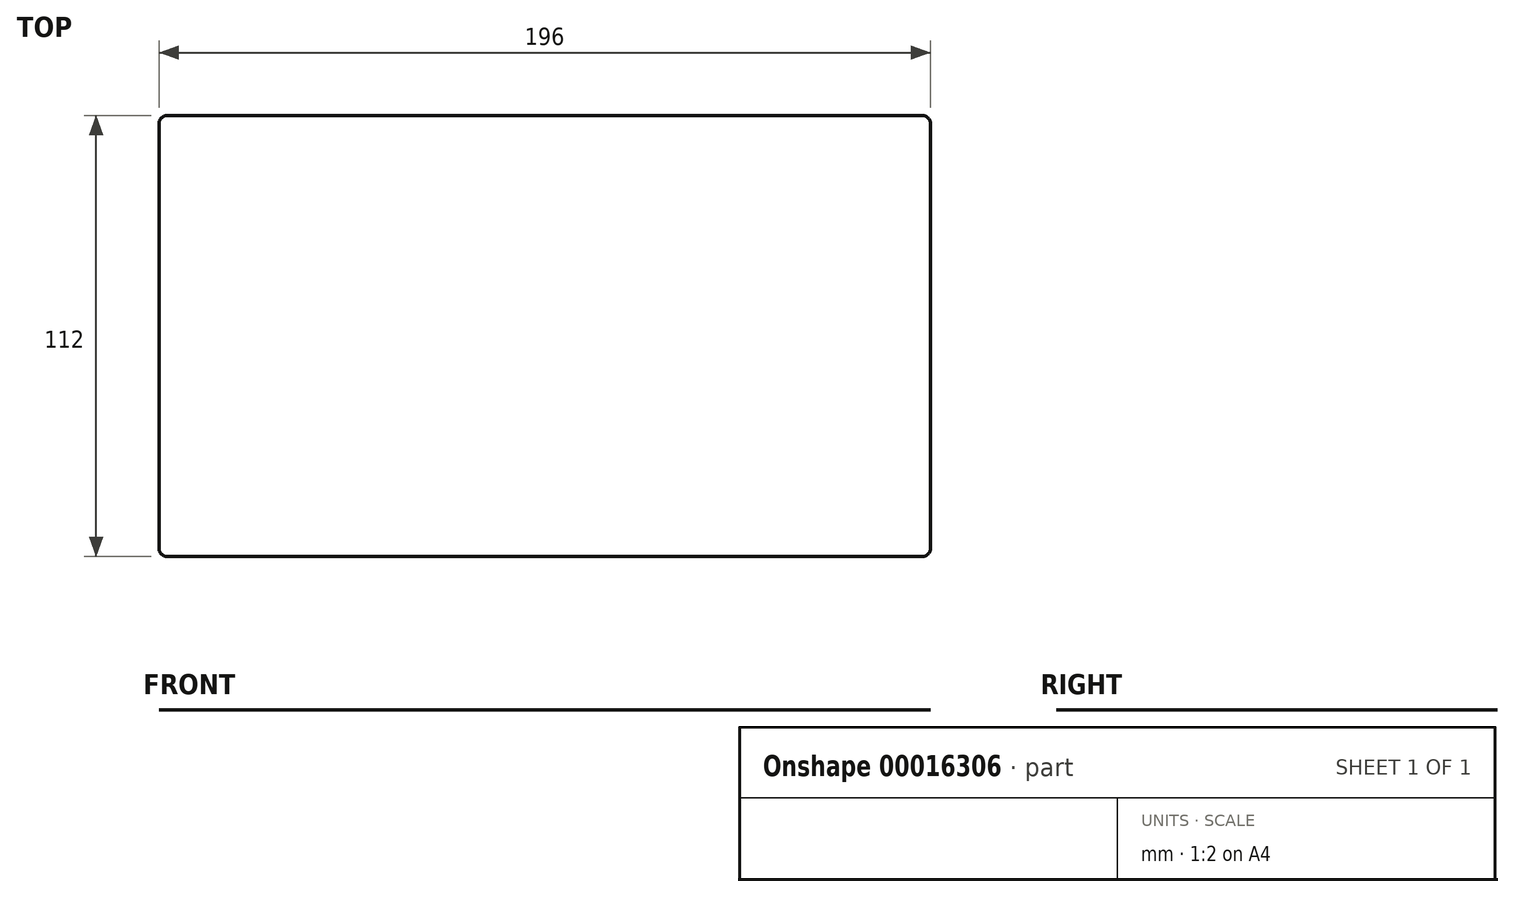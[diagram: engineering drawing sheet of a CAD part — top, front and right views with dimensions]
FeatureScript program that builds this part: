
annotation { "Feature Type Name" : "Feature", "Feature Type Description" : "" }
export const myFeature = defineFeature(function(context is Context, id is Id, definition is map)
    precondition{}
    {
        {
            var Q0;
            Q0=qCreatedBy(makeId("Top.planeOp"),FACE);
            var sketch = newSketch(context, id + "F0", { "sketchPlane" : qUnion([Q0])});
            skLineSegment(sketch, "E0.bottom", {"start": v(96, 54) * mm, "end": v(-96, 54) * mm, "construction": true});
            skLineSegment(sketch, "E0.top", {"start": v(96, -54) * mm, "end": v(-96, -54) * mm, "construction": true});
            skLineSegment(sketch, "E0.left", {"start": v(96, 54) * mm, "end": v(96, -54) * mm, "construction": true});
            skLineSegment(sketch, "E0.right", {"start": v(-96, 54) * mm, "end": v(-96, -54) * mm, "construction": true});
            skPoint(sketch, "E0.middle", {"position": v(0, 0) * mm});
            skLineSegment(sketch, "E1.0", {"start": v(96, 56) * mm, "end": v(-96, 56) * mm});
            skLineSegment(sketch, "E1.1", {"start": v(98, 54) * mm, "end": v(98, -54) * mm});
            skLineSegment(sketch, "E1.2", {"start": v(96, -56) * mm, "end": v(-96, -56) * mm});
            skLineSegment(sketch, "E1.3", {"start": v(-98, 54) * mm, "end": v(-98, -54) * mm});
            skPoint(sketch, "E2.visualSharp", {"position": v(-98, 56) * mm});
            skArc(sketch, "E2.filletArc", {"start": v(-96, 56) * mm, "mid": v(-97.41, 55.41) * mm, "end": v(-98, 54) * mm});
            skPoint(sketch, "E3.visualSharp", {"position": v(-98, -56) * mm});
            skArc(sketch, "E3.filletArc", {"start": v(-98, -54) * mm, "mid": v(-97.41, -55.41) * mm, "end": v(-96, -56) * mm});
            skPoint(sketch, "E4.visualSharp", {"position": v(98, -56) * mm});
            skArc(sketch, "E4.filletArc", {"start": v(96, -56) * mm, "mid": v(97.41, -55.41) * mm, "end": v(98, -54) * mm});
            skPoint(sketch, "E5.visualSharp", {"position": v(98, 56) * mm});
            skArc(sketch, "E5.filletArc", {"start": v(98, 54) * mm, "mid": v(97.41, 55.41) * mm, "end": v(96, 56) * mm});
            skSolve(sketch);
        }
        {
            var Q0;
            Q0=makeQuery(id+"F0.imprint","IMPRINT",FACE,{"disambiguationData":[TD([[makeQuery(id+"F0.imprint","IMPRINT",EDGE,{"derivedFrom":sQuery(id+"F0.wireOp",EDGE,"E1.0")}),1.0]])]});
            extrude(context, id + "F1", {"entities" : qUnion([Q0]), "depth" : 1 / 203.2 * mm});
        }
    });
